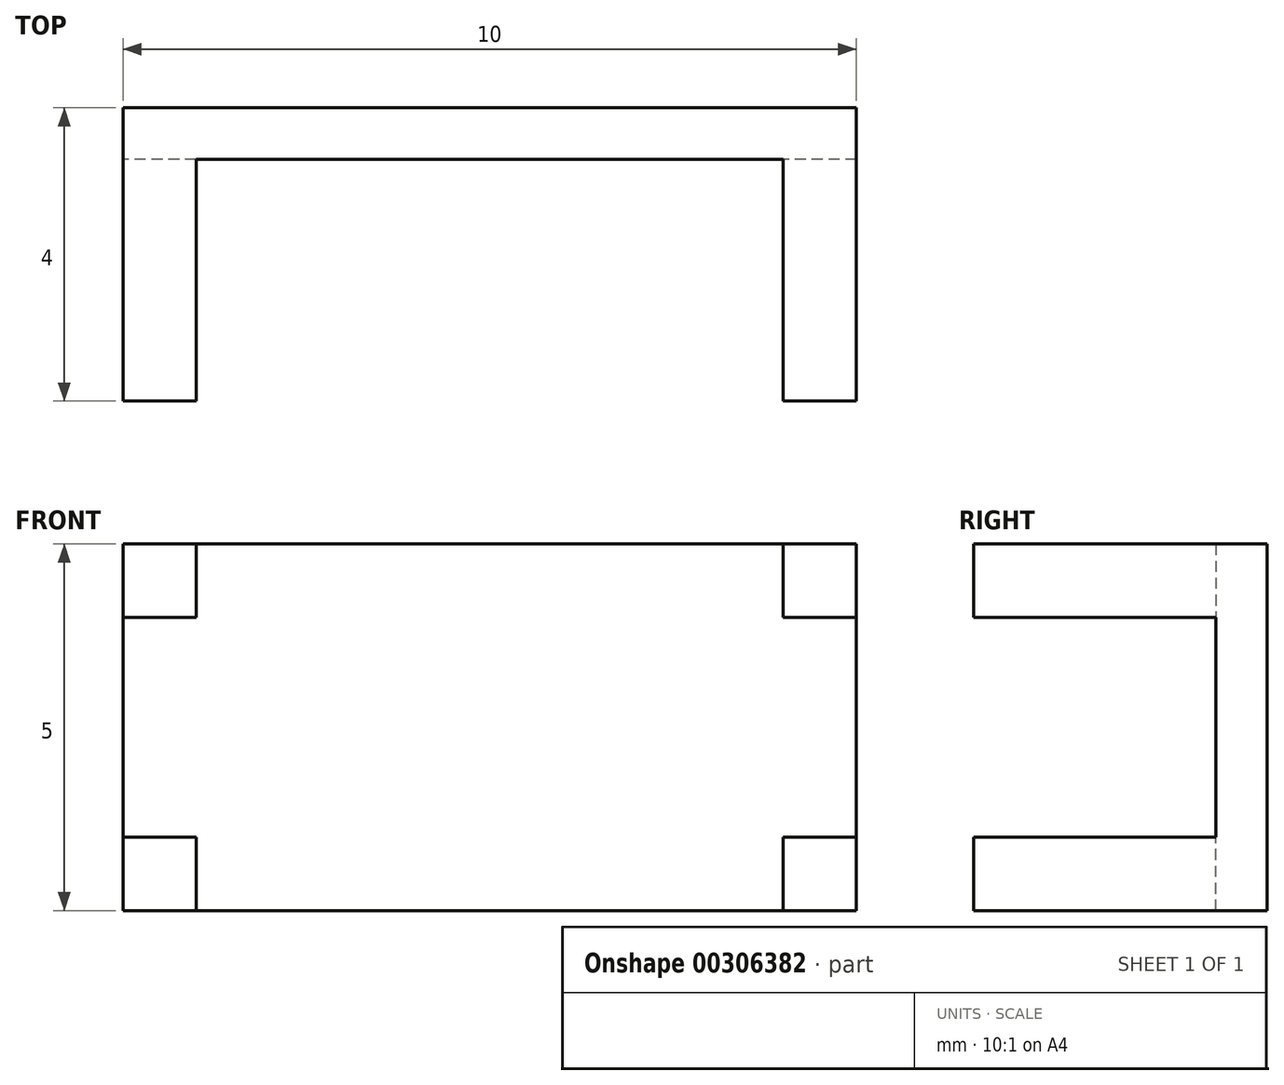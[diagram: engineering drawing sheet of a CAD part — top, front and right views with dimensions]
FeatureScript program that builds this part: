
annotation { "Feature Type Name" : "Feature", "Feature Type Description" : "" }
export const myFeature = defineFeature(function(context is Context, id is Id, definition is map)
    precondition{}
    {
        {
            var Q0;
            Q0=qCreatedBy(makeId("Front.planeOp"),FACE);
            var sketch = newSketch(context, id + "F0", { "sketchPlane" : qUnion([Q0])});
            skLineSegment(sketch, "E0.bottom", {"start": v(31.1, 0) * mm, "end": v(-68.9, 0) * mm});
            skLineSegment(sketch, "E0.top", {"start": v(31.1, 50) * mm, "end": v(-68.9, 50) * mm});
            skLineSegment(sketch, "E0.left", {"start": v(31.1, 0) * mm, "end": v(31.1, 50) * mm});
            skLineSegment(sketch, "E0.right", {"start": v(-68.9, 0) * mm, "end": v(-68.9, 50) * mm});
            skSolve(sketch);
        }
        {
            var Q0;
            Q0=makeQuery(id+"F0.imprint","IMPRINT",FACE,{"disambiguationData":[TD([[makeQuery(id+"F0.imprint","IMPRINT",EDGE,{"derivedFrom":sQuery(id+"F0.wireOp",EDGE,"E0.bottom")}),-1.0]])]});
            extrude(context, id + "F1", {"entities" : qUnion([Q0]), "depth" : 25 * mm});
        }
        {
            var Q0;
            Q0=makeQuery(id+"F1.opExtrude","CAP_FACE",FACE,{"disambiguationData":[OSD([sQuery(id+"F0.wireOp",EDGE,"E0.bottom"),sQuery(id+"F0.wireOp",EDGE,"E0.top"),sQuery(id+"F0.wireOp",EDGE,"E0.left"),sQuery(id+"F0.wireOp",EDGE,"E0.right")])],"isStart":false});
            var sketch = newSketch(context, id + "F2", { "sketchPlane" : qUnion([Q0])});
            skLineSegment(sketch, "E1", {"start": v(-68.9, 0) * mm, "end": v(-58.9, 0) * mm});
            skLineSegment(sketch, "E2", {"start": v(-58.9, 0) * mm, "end": v(-58.9, 10) * mm});
            skLineSegment(sketch, "E3", {"start": v(-58.9, 10) * mm, "end": v(-68.9, 10) * mm});
            skLineSegment(sketch, "E4", {"start": v(-68.9, 0) * mm, "end": v(-68.9, 10) * mm});
            skLineSegment(sketch, "E5", {"start": v(-68.9, 50) * mm, "end": v(-58.9, 50) * mm});
            skLineSegment(sketch, "E6", {"start": v(-58.9, 50) * mm, "end": v(-58.9, 40) * mm});
            skLineSegment(sketch, "E7", {"start": v(-58.9, 40) * mm, "end": v(-68.9, 40) * mm});
            skLineSegment(sketch, "E8", {"start": v(-68.9, 40) * mm, "end": v(-68.9, 50) * mm});
            skLineSegment(sketch, "E9", {"start": v(31.1, 50) * mm, "end": v(31.1, 40) * mm});
            skLineSegment(sketch, "E10", {"start": v(31.1, 40) * mm, "end": v(21.1, 40) * mm});
            skLineSegment(sketch, "E11", {"start": v(21.1, 40) * mm, "end": v(21.1, 50) * mm});
            skLineSegment(sketch, "E12", {"start": v(21.1, 50) * mm, "end": v(31.1, 50) * mm});
            skLineSegment(sketch, "E13", {"start": v(31.1, 0) * mm, "end": v(31.1, 10) * mm});
            skLineSegment(sketch, "E14", {"start": v(31.1, 10) * mm, "end": v(21.1, 10) * mm});
            skLineSegment(sketch, "E15", {"start": v(21.1, 10) * mm, "end": v(21.1, 0) * mm});
            skLineSegment(sketch, "E16", {"start": v(21.1, 0) * mm, "end": v(31.1, 0) * mm});
            skSolve(sketch);
        }
        {
            var Q0;
            Q0=qSketchRegion(id+"F2",true);
            extrude(context, id + "F3", {"entities" : qUnion([Q0]), "operationType" : NewBodyOperationType.ADD, "depth" : 15 * mm});
        }
        {
            var Q0;
            Q0=makeQuery(id+"F1.opExtrude","CAP_FACE",FACE,{"disambiguationData":[OSD([sQuery(id+"F0.wireOp",EDGE,"E0.bottom"),sQuery(id+"F0.wireOp",EDGE,"E0.top"),sQuery(id+"F0.wireOp",EDGE,"E0.left"),sQuery(id+"F0.wireOp",EDGE,"E0.right")])],"isStart":false});
            extrude(context, id + "F4", {"entities" : qUnion([Q0]), "operationType" : NewBodyOperationType.REMOVE, "oppositeDirection" : true, "depth" : 18 * mm});
        }
        {
            var Q0;
            Q0=makeQuery(id+"F1.opExtrude","SWEPT_BODY",BODY,{"disambiguationData":[OSD([sQuery(id+"F0.wireOp",EDGE,"E0.bottom"),sQuery(id+"F0.wireOp",EDGE,"E0.top"),sQuery(id+"F0.wireOp",EDGE,"E0.left"),sQuery(id+"F0.wireOp",EDGE,"E0.right")])]});
            var Q1;
            Q1=qCreatedBy(makeId("Origin.pointOp"),VERTEX);
            var Q2;
            Q2=qCreatedBy(makeId("Origin.pointOp"),VERTEX);
            transform(context, id + "F5", {"entities" : qUnion([Q0]), "transformType" : TransformType.SCALE_UNIFORMLY, "scale" : 0.1, "scalePoint" : qUnion([Q2]), "makeCopy" : false});
        }
    });
